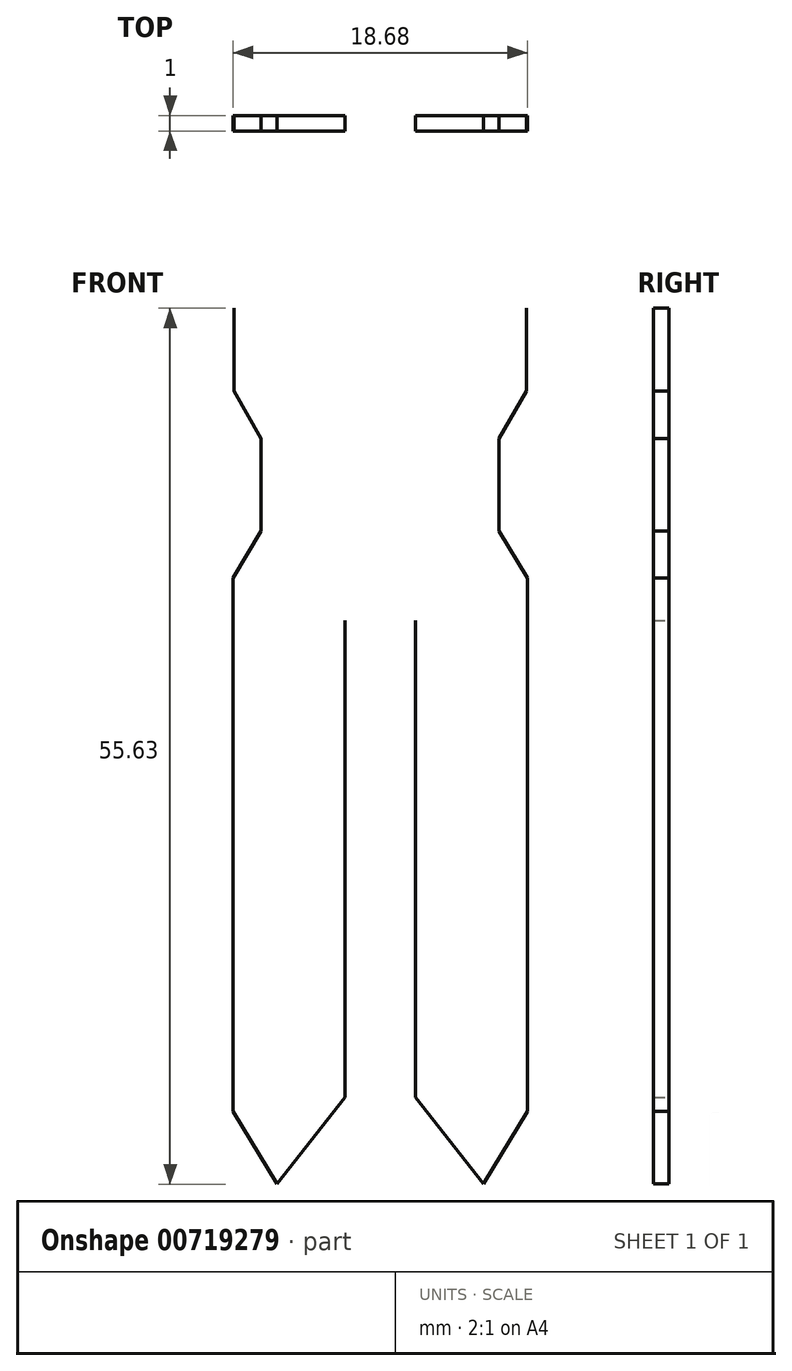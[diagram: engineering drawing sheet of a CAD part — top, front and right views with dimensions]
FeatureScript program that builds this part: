
annotation { "Feature Type Name" : "Feature", "Feature Type Description" : "" }
export const myFeature = defineFeature(function(context is Context, id is Id, definition is map)
    precondition{}
    {
        {
            var Q0;
            Q0=qCreatedBy(makeId("Front.planeOp"),FACE);
            var sketch = newSketch(context, id + "F0", { "sketchPlane" : qUnion([Q0])});
            skLineSegment(sketch, "E0", {"start": v(0, 0) * mm, "end": v(19.25, 0) * mm});
            skLineSegment(sketch, "E1", {"start": v(19.25, 0) * mm, "end": v(19.25, -5.25) * mm});
            skLineSegment(sketch, "E2", {"start": v(19.25, -5.25) * mm, "end": v(17.51, -8.29) * mm});
            skLineSegment(sketch, "E3", {"start": v(17.51, -8.29) * mm, "end": v(17.51, -14.14) * mm});
            skLineSegment(sketch, "E4", {"start": v(17.51, -14.14) * mm, "end": v(19.3, -17.15) * mm});
            skLineSegment(sketch, "E5", {"start": v(19.3, -17.15) * mm, "end": v(19.3, -20.7) * mm});
            skLineSegment(sketch, "E6", {"start": v(19.3, -20.7) * mm, "end": v(19.3, -51) * mm});
            skLineSegment(sketch, "E7", {"start": v(19.3, -51) * mm, "end": v(16.52, -55.63) * mm});
            skLineSegment(sketch, "E8", {"start": v(12.2, -50.12) * mm, "end": v(12.2, -19.82) * mm});
            skLineSegment(sketch, "E9", {"start": v(9.96, -70.53) * mm, "end": v(9.96, 20.23) * mm, "construction": true});
            skLineSegment(sketch, "E10.MirrorCS", {"start": v(0.62, -17.15) * mm, "end": v(0.62, -20.7) * mm});
            skLineSegment(sketch, "E11.MirrorCS", {"start": v(0.62, -20.7) * mm, "end": v(0.62, -51) * mm});
            skLineSegment(sketch, "E12.MirrorCS", {"start": v(0.62, -51) * mm, "end": v(3.4, -55.63) * mm});
            skLineSegment(sketch, "E13.MirrorCS", {"start": v(7.72, -50.12) * mm, "end": v(7.72, -19.82) * mm});
            skLineSegment(sketch, "E14", {"start": v(0.62, -51) * mm, "end": v(7.72, -50.12) * mm, "construction": true});
            skLineSegment(sketch, "E15", {"start": v(12.2, -50.12) * mm, "end": v(19.3, -51) * mm, "construction": true});
            skLineSegment(sketch, "E16.MirrorCS", {"start": v(0.66, 0) * mm, "end": v(0.66, -5.25) * mm});
            skLineSegment(sketch, "E17.MirrorCS", {"start": v(0.66, -5.25) * mm, "end": v(2.4, -8.29) * mm});
            skLineSegment(sketch, "E18.MirrorCS", {"start": v(2.4, -8.29) * mm, "end": v(2.4, -14.14) * mm});
            skLineSegment(sketch, "E19.MirrorCS", {"start": v(2.4, -14.14) * mm, "end": v(0.62, -17.15) * mm});
            skLineSegment(sketch, "E20", {"start": v(3.4, -55.63) * mm, "end": v(7.72, -50.12) * mm});
            skLineSegment(sketch, "E21", {"start": v(12.2, -50.12) * mm, "end": v(16.52, -55.63) * mm});
            skCircle(sketch, "E22", {"center": v(4.08, -2.26) * mm, "radius": 1.8 * mm});
            skCircle(sketch, "E23.MirrorC", {"center": v(15.83, -2.26) * mm, "radius": 1.8 * mm});
            skArc(sketch, "E24", {"start": v(12.2, -20.1) * mm, "mid": v(9.96, -17.56) * mm, "end": v(7.72, -20.1) * mm});
            skSolve(sketch);
        }
        {
            var Q0;
            Q0=sQuery(id+"F0.wireOp",EDGE,"E1");
            var Q1;
            Q1=sQuery(id+"F0.wireOp",EDGE,"E2");
            var Q2;
            Q2=sQuery(id+"F0.wireOp",EDGE,"E3");
            var Q3;
            Q3=sQuery(id+"F0.wireOp",EDGE,"E4");
            var Q4;
            Q4=sQuery(id+"F0.wireOp",EDGE,"E6");
            var Q5;
            Q5=sQuery(id+"F0.wireOp",EDGE,"E5");
            var Q6;
            Q6=sQuery(id+"F0.wireOp",EDGE,"E7");
            var Q7;
            Q7=sQuery(id+"F0.wireOp",EDGE,"E21");
            var Q8;
            Q8=sQuery(id+"F0.wireOp",EDGE,"E8");
            var Q9;
            Q9=sQuery(id+"F0.wireOp",EDGE,"E13.MirrorCS");
            var Q10;
            Q10=sQuery(id+"F0.wireOp",EDGE,"E20");
            var Q11;
            Q11=sQuery(id+"F0.wireOp",EDGE,"E12.MirrorCS");
            var Q12;
            Q12=sQuery(id+"F0.wireOp",EDGE,"E11.MirrorCS");
            var Q13;
            Q13=sQuery(id+"F0.wireOp",EDGE,"E10.MirrorCS");
            var Q14;
            Q14=sQuery(id+"F0.wireOp",EDGE,"E19.MirrorCS");
            var Q15;
            Q15=sQuery(id+"F0.wireOp",EDGE,"E18.MirrorCS");
            var Q16;
            Q16=sQuery(id+"F0.wireOp",EDGE,"E17.MirrorCS");
            var Q17;
            Q17=sQuery(id+"F0.wireOp",EDGE,"E16.MirrorCS");
            extrude(context, id + "F1", {"bodyType" : ToolBodyType.SURFACE, "surfaceEntities" : qUnion([Q0, Q1, Q2, Q3, Q4, Q5, Q6, Q7, Q8, Q9, Q10, Q11, Q12, Q13, Q14, Q15, Q16, Q17]), "oppositeDirection" : true, "depth" : 1 * mm, "offsetDistance" : 25 * mm});
        }
    });
